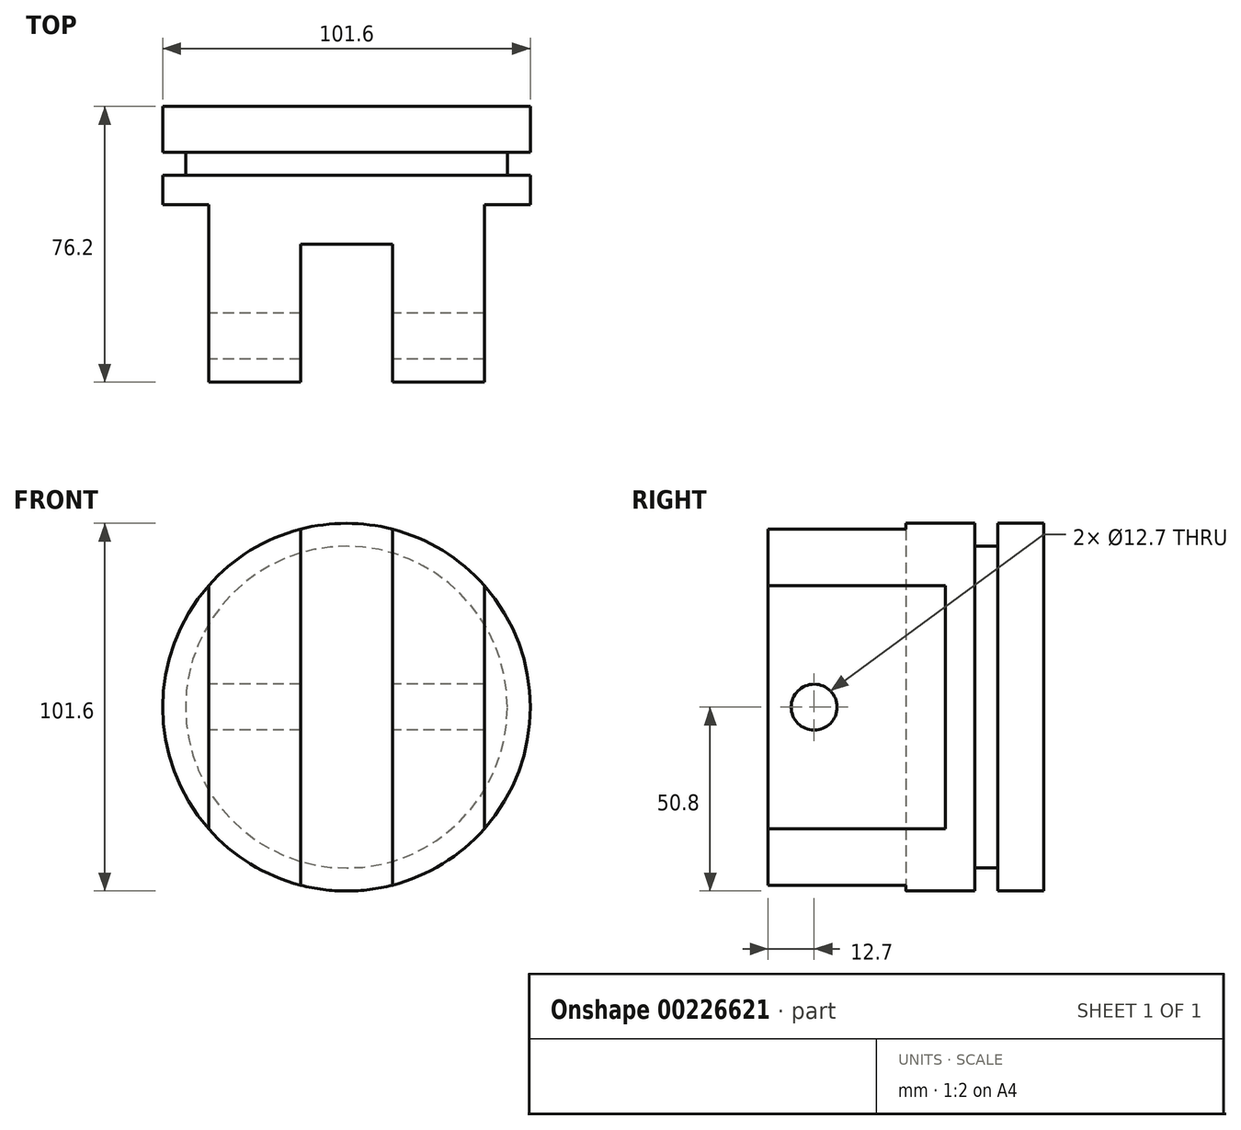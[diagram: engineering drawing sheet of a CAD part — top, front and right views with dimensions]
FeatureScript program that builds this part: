
annotation { "Feature Type Name" : "Feature", "Feature Type Description" : "" }
export const myFeature = defineFeature(function(context is Context, id is Id, definition is map)
    precondition{}
    {
        {
            var Q0;
            Q0=qCreatedBy(makeId("Top.planeOp"),FACE);
            var sketch = newSketch(context, id + "F0", { "sketchPlane" : qUnion([Q0])});
            skLineSegment(sketch, "E0.bottom", {"start": v(0, 0) * mm, "end": v(50.8, 0) * mm});
            skLineSegment(sketch, "E0.top", {"start": v(0, 76.2) * mm, "end": v(50.8, 76.2) * mm});
            skLineSegment(sketch, "E0.left", {"start": v(0, 0) * mm, "end": v(0, 76.2) * mm});
            skLineSegment(sketch, "E0.right", {"start": v(50.8, 0) * mm, "end": v(50.8, 57.15) * mm});
            skLineSegment(sketch, "E1.bottom", {"start": v(50.8, 63.5) * mm, "end": v(44.45, 63.5) * mm});
            skLineSegment(sketch, "E1.top", {"start": v(50.8, 57.15) * mm, "end": v(44.45, 57.15) * mm});
            skLineSegment(sketch, "E1.right", {"start": v(44.45, 63.5) * mm, "end": v(44.45, 57.15) * mm});
            skLineSegment(sketch, "E2.trimOffspring", {"start": v(50.8, 63.5) * mm, "end": v(50.8, 76.2) * mm});
            skLineSegment(sketch, "E3", {"start": v(0, -9.78) * mm, "end": v(0, 90.76) * mm, "construction": true});
            skSolve(sketch);
        }
        {
            var Q0;
            Q0=makeQuery(id+"F0.imprint","IMPRINT",FACE,{"disambiguationData":[TD([[makeQuery(id+"F0.imprint","IMPRINT",EDGE,{"derivedFrom":sQuery(id+"F0.wireOp",EDGE,"E0.bottom")}),1.0]])]});
            var Q1;
            Q1=sQuery(id+"F0.wireOp",EDGE,"E0.right");
            var Q2;
            Q2=sQuery(id+"F0.wireOp",EDGE,"E0.bottom");
            var Q3;
            Q3=sQuery(id+"F0.wireOp",EDGE,"E3");
            revolve(context, id + "F1", {"entities" : qUnion([Q0]), "surfaceEntities" : qUnion([Q1, Q2]), "axis" : qUnion([Q3]), "revolveType" : RevolveType.FULL});
        }
        {
            var Q0;
            Q0=qCreatedBy(makeId("Top.planeOp"),FACE);
            var sketch = newSketch(context, id + "F2", { "sketchPlane" : qUnion([Q0])});
            skLineSegment(sketch, "E4.bottom", {"start": v(-12.7, 0) * mm, "end": v(12.7, 0) * mm});
            skLineSegment(sketch, "E4.top", {"start": v(-12.7, 38.1) * mm, "end": v(12.7, 38.1) * mm});
            skLineSegment(sketch, "E4.left", {"start": v(-12.7, 0) * mm, "end": v(-12.7, 38.1) * mm});
            skLineSegment(sketch, "E4.right", {"start": v(12.7, 0) * mm, "end": v(12.7, 38.1) * mm});
            skSolve(sketch);
        }
        {
            var Q0;
            Q0 = qSketchRegion(id + "F2", true);
            extrude(context, id + "F3", {"entities" : qUnion([Q0]), "operationType" : NewBodyOperationType.REMOVE, "depth" : 146.8 * mm, "symmetric" : true});
        }
        {
            var Q0;
            Q0=makeQuery(id+"F3.boolean.opBoolean","SPLIT",FACE,{"disambiguationData":[TD([makeQuery(id+"F3.opExtrude","SWEPT_FACE",FACE,{"disambiguationData":[OSD([sQuery(id+"F2.wireOp",EDGE,"E4.left")])]})])],"derivedFrom":makeQuery(id+"F1.opRevolve","SWEPT_FACE",FACE,{"disambiguationData":[OSD([sQuery(id+"F0.wireOp",EDGE,"E0.bottom")])]})});
            var sketch = newSketch(context, id + "F4", { "sketchPlane" : qUnion([Q0])});
            skLineSegment(sketch, "E5.bottom", {"start": v(-38.1, 56.33) * mm, "end": v(-88.95, 56.33) * mm});
            skLineSegment(sketch, "E5.top", {"start": v(-38.1, -38.2) * mm, "end": v(-88.95, -38.2) * mm});
            skLineSegment(sketch, "E5.left", {"start": v(-38.1, 56.33) * mm, "end": v(-38.1, -38.2) * mm});
            skLineSegment(sketch, "E5.right", {"start": v(-88.95, 56.33) * mm, "end": v(-88.95, -38.2) * mm});
            skLineSegment(sketch, "E6.bottom", {"start": v(38.1, 40.65) * mm, "end": v(76.74, 40.65) * mm});
            skLineSegment(sketch, "E6.top", {"start": v(38.1, -42.98) * mm, "end": v(76.74, -42.98) * mm});
            skLineSegment(sketch, "E6.left", {"start": v(38.1, 40.65) * mm, "end": v(38.1, -42.98) * mm});
            skLineSegment(sketch, "E6.right", {"start": v(76.74, 40.65) * mm, "end": v(76.74, -42.98) * mm});
            skSolve(sketch);
        }
        {
            var Q0;
            Q0 = qSketchRegion(id + "F4", true);
            extrude(context, id + "F5", {"entities" : qUnion([Q0]), "operationType" : NewBodyOperationType.REMOVE, "oppositeDirection" : true, "depth" : 49.02 * mm});
        }
        {
            var Q0;
            Q0=makeQuery(id+"F5.boolean.opBoolean","COPY",FACE,{"derivedFrom":makeQuery(id+"F5.opExtrude","SWEPT_FACE",FACE,{"disambiguationData":[OSD([sQuery(id+"F4.wireOp",EDGE,"E5.left")])]})});
            var sketch = newSketch(context, id + "F6", { "sketchPlane" : qUnion([Q0])});
            skCircle(sketch, "E7", {"center": v(-12.7, 0) * mm, "radius": 6.35 * mm});
            skSolve(sketch);
        }
        {
            var Q0;
            Q0 = qSketchRegion(id + "F6", true);
            extrude(context, id + "F7", {"entities" : qUnion([Q0]), "operationType" : NewBodyOperationType.REMOVE, "oppositeDirection" : true, "depth" : 140.46 * mm});
        }
    });
